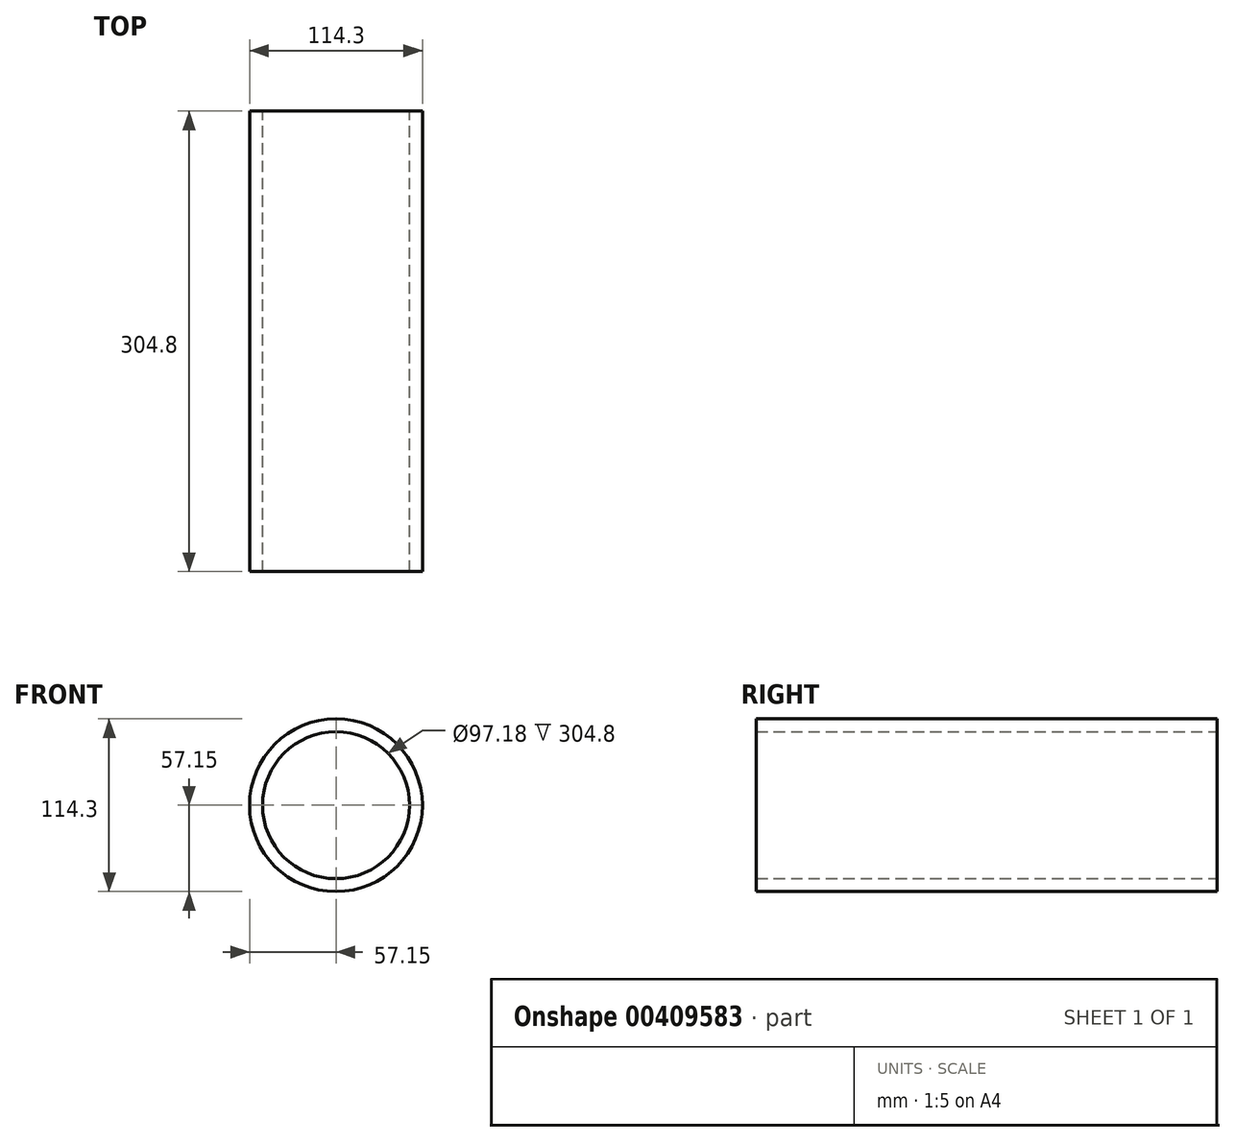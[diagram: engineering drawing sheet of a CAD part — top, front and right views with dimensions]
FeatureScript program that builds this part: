
annotation { "Feature Type Name" : "Feature", "Feature Type Description" : "" }
export const myFeature = defineFeature(function(context is Context, id is Id, definition is map)
    precondition{}
    {
        {
            var Q0;
            Q0=qCreatedBy(makeId("Front.planeOp"),FACE);
            var sketch = newSketch(context, id + "F0", { "sketchPlane" : qUnion([Q0])});
            skCircle(sketch, "E0", {"center": v(0, 0) * mm, "radius": 57.15 * mm});
            skCircle(sketch, "E1", {"center": v(0, 0) * mm, "radius": 48.6 * mm});
            skSolve(sketch);
        }
        {
            var Q0;
            Q0=makeQuery(id+"F0.imprint","IMPRINT",FACE,{"disambiguationData":[TD([[makeQuery(id+"F0.imprint","IMPRINT",EDGE,{"derivedFrom":sQuery(id+"F0.wireOp",EDGE,"E0")}),1.0]])]});
            extrude(context, id + "F1", {"entities" : qUnion([Q0]), "endBound" : BoundingType.SYMMETRIC, "depth" : 304.8 * mm});
        }
    });
